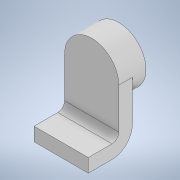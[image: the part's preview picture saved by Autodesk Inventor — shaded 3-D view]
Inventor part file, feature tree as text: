
AUTODESK INVENTOR PART (.ipt)
format: ipt  version: 2022.2 (Build 262287030, 287C)  size: 115,200 bytes
history: native  units: in
note: dims shown in document units (in); Inventor stores cm internally (conversion verified against a paired STEP export)
features: extrude x2, sketch x2
ambient origin geometry x8: Origin, YZ Plane, XZ Plane, XY Plane, X Axis, Y Axis, Z Axis, Center Point
bodies: Solid1 (feature_tree)
feature tree (4):
  extrude  "Extrusion1"  Depth=2.0in TaperAngle=0.0deg
  extrude  "Extrusion2"  Depth=0.5in
  sketch  "Sketch1"  dims[d0=4.0in d1=2.0in d2=0.0in]
  sketch  "Sketch2"  dims[d3=2.25in d4=0.5in d5=1.0in d6=1.5in d7=5.0in d8=4.0in d9=0.0in]
